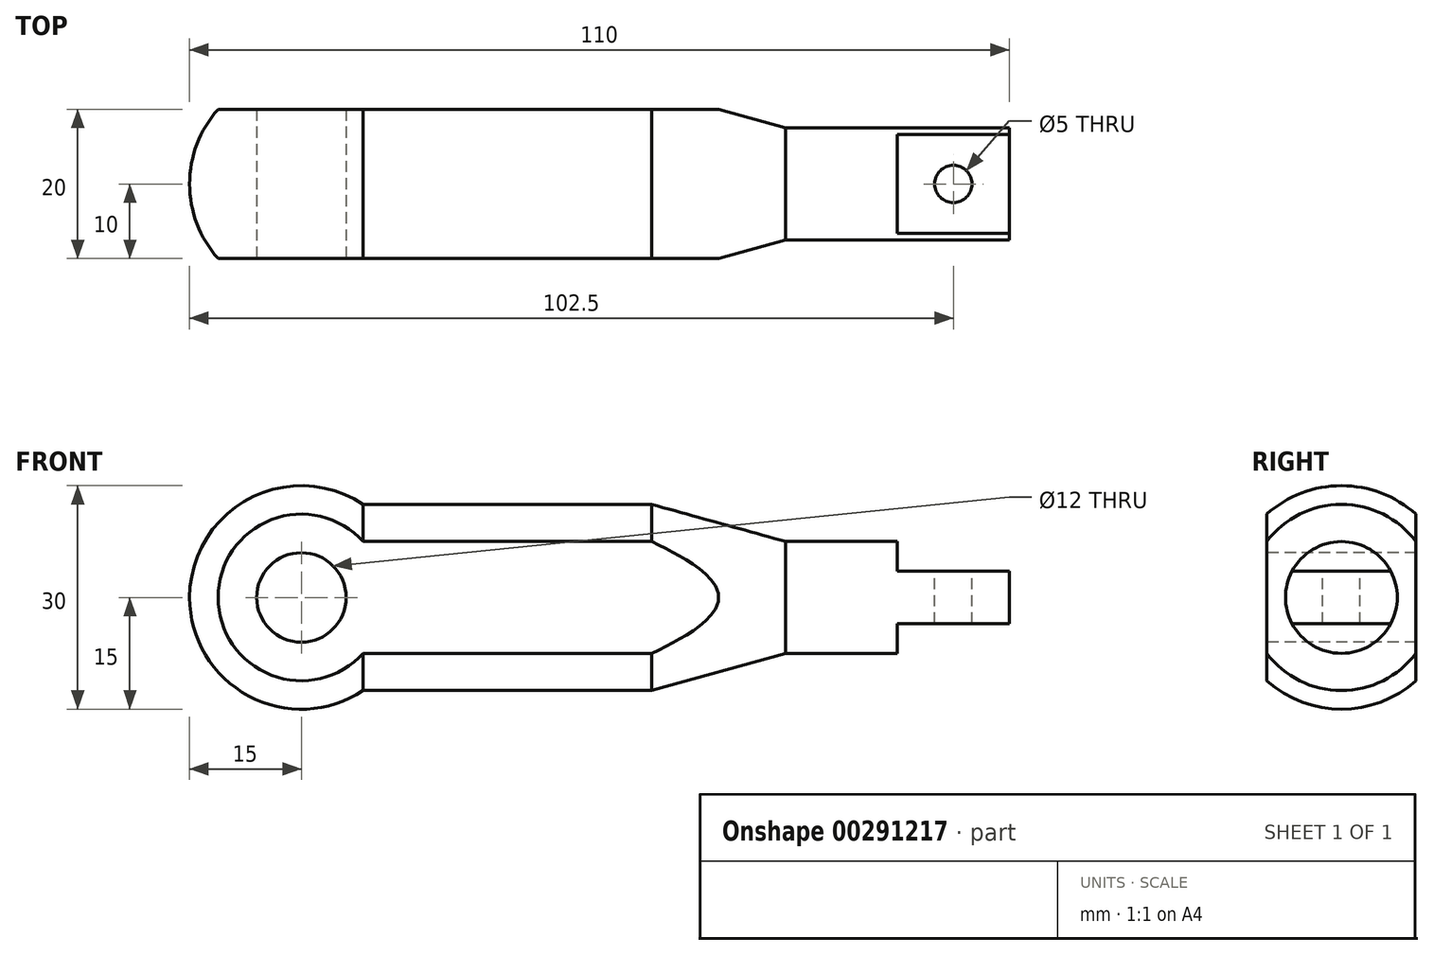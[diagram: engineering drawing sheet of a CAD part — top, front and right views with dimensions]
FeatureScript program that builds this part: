
annotation { "Feature Type Name" : "Feature", "Feature Type Description" : "" }
export const myFeature = defineFeature(function(context is Context, id is Id, definition is map)
    precondition{}
    {
        {
            var Q0;
            Q0=qCreatedBy(makeId("Front.planeOp"),FACE);
            var sketch = newSketch(context, id + "F0", { "sketchPlane" : qUnion([Q0])});
            skLineSegment(sketch, "E0", {"start": v(0, 0) * mm, "end": v(118.77, 0) * mm, "construction": true});
            skArc(sketch, "E1", {"start": v(-15, 0) * mm, "mid": v(-7.1, 13.22) * mm, "end": v(8.3, 12.5) * mm});
            skLineSegment(sketch, "E2", {"start": v(8.3, 12.5) * mm, "end": v(47, 12.5) * mm});
            skLineSegment(sketch, "E3", {"start": v(47, 12.5) * mm, "end": v(65, 7.5) * mm});
            skLineSegment(sketch, "E4", {"start": v(65, 7.5) * mm, "end": v(95, 7.5) * mm});
            skLineSegment(sketch, "E5", {"start": v(95, 7.5) * mm, "end": v(95, 0) * mm});
            skLineSegment(sketch, "E6", {"start": v(95, 0) * mm, "end": v(-15, 0) * mm});
            skSolve(sketch);
        }
        {
            var Q0;
            Q0 = qSketchRegion(id + "F0", true);
            var Q1;
            Q1=sQuery(id+"F0.wireOp",EDGE,"E0");
            revolve(context, id + "F1", {"entities" : qUnion([Q0]), "axis" : qUnion([Q1]), "revolveType" : RevolveType.FULL});
        }
        {
            var Q0;
            Q0=qCreatedBy(makeId("Front.planeOp"),FACE);
            var sketch = newSketch(context, id + "F2", { "sketchPlane" : qUnion([Q0])});
            skLineSegment(sketch, "E7.bottom", {"start": v(80, 3.5) * mm, "end": v(95, 3.5) * mm});
            skLineSegment(sketch, "E7.left", {"start": v(80, 3.5) * mm, "end": v(80, 7.5) * mm});
            skLineSegment(sketch, "E7.right", {"start": v(95, 3.5) * mm, "end": v(95, 7.5) * mm});
            skLineSegment(sketch, "E8", {"start": v(80, 7.5) * mm, "end": v(95, 7.5) * mm});
            skLineSegment(sketch, "E9", {"start": v(95, -7.5) * mm, "end": v(80, -7.5) * mm});
            skLineSegment(sketch, "E10", {"start": v(64.14, 0) * mm, "end": v(100.56, 0) * mm, "construction": true});
            skLineSegment(sketch, "E11.bottom", {"start": v(80, -3.5) * mm, "end": v(95, -3.5) * mm});
            skLineSegment(sketch, "E11.top", {"start": v(80, -7.5) * mm, "end": v(95, -7.5) * mm});
            skLineSegment(sketch, "E11.left", {"start": v(80, -3.5) * mm, "end": v(80, -7.5) * mm});
            skLineSegment(sketch, "E11.right", {"start": v(95, -3.5) * mm, "end": v(95, -7.5) * mm});
            skSolve(sketch);
        }
        {
            var Q0;
            Q0 = qSketchRegion(id + "F2", true);
            extrude(context, id + "F3", {"entities" : qUnion([Q0]), "operationType" : NewBodyOperationType.REMOVE, "oppositeDirection" : true, "depth" : 25 * mm, "hasSecondDirection" : true, "secondDirectionOppositeDirection" : false, "secondDirectionDepth" : 25 * mm});
        }
        {
            var Q0;
            Q0=qCreatedBy(makeId("Right.planeOp"),FACE);
            var sketch = newSketch(context, id + "F4", { "sketchPlane" : qUnion([Q0])});
            skArc(sketch, "E12", {"start": v(-10, 11.18) * mm, "mid": v(-15, 0) * mm, "end": v(-10, -11.18) * mm});
            skLineSegment(sketch, "E13", {"start": v(-10, 11.18) * mm, "end": v(-10, -11.18) * mm});
            skLineSegment(sketch, "E14", {"start": v(10, 11.18) * mm, "end": v(10, -11.18) * mm});
            skLineSegment(sketch, "E15", {"start": v(0, 23.88) * mm, "end": v(0, -22.08) * mm, "construction": true});
            skArc(sketch, "E16.trimOffspring", {"start": v(10, -11.18) * mm, "mid": v(15, 0) * mm, "end": v(10, 11.18) * mm});
            skSolve(sketch);
        }
        {
            var Q0;
            Q0 = qSketchRegion(id + "F4", true);
            extrude(context, id + "F5", {"entities" : qUnion([Q0]), "operationType" : NewBodyOperationType.REMOVE, "endBound" : BoundingType.THROUGH_ALL, "depth" : 25 * mm, "hasSecondDirection" : true, "secondDirectionOppositeDirection" : true, "secondDirectionDepth" : 25 * mm});
        }
        {
            var Q0;
            Q0=makeQuery(id+"F5.boolean.opBoolean","COPY",FACE,{"derivedFrom":makeQuery(id+"F5.opExtrude","SWEPT_FACE",FACE,{"disambiguationData":[OSD([sQuery(id+"F4.wireOp",EDGE,"E13")])]})});
            var sketch = newSketch(context, id + "F6", { "sketchPlane" : qUnion([Q0])});
            skCircle(sketch, "E17", {"center": v(0, 0) * mm, "radius": 6 * mm});
            skSolve(sketch);
        }
        {
            var Q0;
            Q0=makeQuery(id+"F3.boolean.opBoolean","COPY",FACE,{"derivedFrom":makeQuery(id+"F3.opExtrude","SWEPT_FACE",FACE,{"disambiguationData":[OSD([sQuery(id+"F2.wireOp",EDGE,"E7.bottom")])]})});
            var sketch = newSketch(context, id + "F7", { "sketchPlane" : qUnion([Q0])});
            skCircle(sketch, "E18", {"center": v(87.5, 0) * mm, "radius": 2.5 * mm});
            skSolve(sketch);
        }
        {
            var Q0;
            Q0 = qSketchRegion(id + "F7", true);
            extrude(context, id + "F8", {"entities" : qUnion([Q0]), "operationType" : NewBodyOperationType.REMOVE, "oppositeDirection" : true, "depth" : 25 * mm});
        }
        {
            var Q0;
            Q0 = qSketchRegion(id + "F6", true);
            extrude(context, id + "F9", {"entities" : qUnion([Q0]), "operationType" : NewBodyOperationType.REMOVE, "oppositeDirection" : true, "depth" : 25 * mm});
        }
    });
